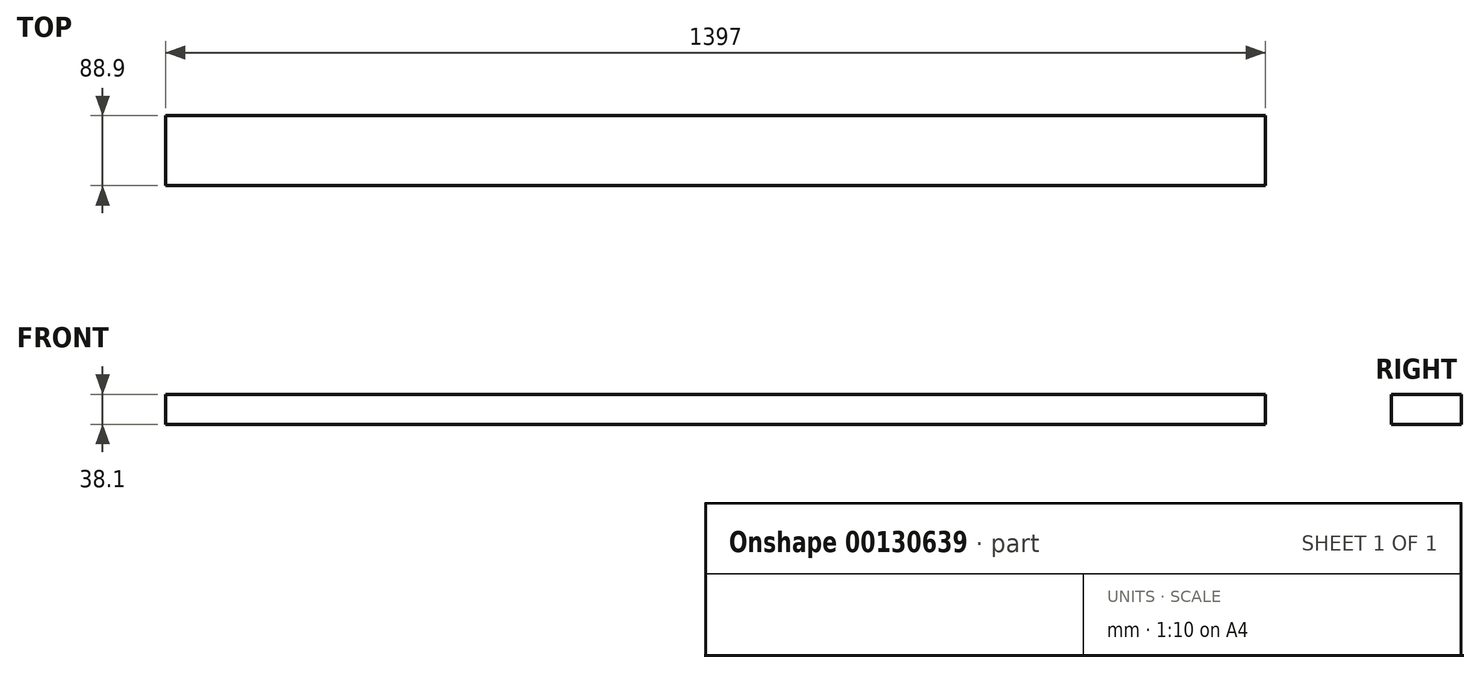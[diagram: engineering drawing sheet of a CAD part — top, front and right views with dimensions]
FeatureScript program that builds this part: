
annotation { "Feature Type Name" : "Feature", "Feature Type Description" : "" }
export const myFeature = defineFeature(function(context is Context, id is Id, definition is map)
    precondition{}
    {
        {
            var Q0;
            Q0=qCreatedBy(makeId("Top.planeOp"),FACE);
            var sketch = newSketch(context, id + "F0", { "sketchPlane" : qUnion([Q0])});
            skLineSegment(sketch, "E0.bottom", {"start": v(0, 0) * mm, "end": v(1397, 0) * mm});
            skLineSegment(sketch, "E0.top", {"start": v(0, 88.9) * mm, "end": v(1397, 88.9) * mm});
            skLineSegment(sketch, "E0.left", {"start": v(0, 0) * mm, "end": v(0, 88.9) * mm});
            skLineSegment(sketch, "E0.right", {"start": v(1397, 0) * mm, "end": v(1397, 88.9) * mm});
            skSolve(sketch);
        }
        {
            var Q0;
            Q0=makeQuery(id+"F0.imprint","IMPRINT",FACE,{"disambiguationData":[TD([[makeQuery(id+"F0.imprint","IMPRINT",EDGE,{"derivedFrom":sQuery(id+"F0.wireOp",EDGE,"E0.bottom")}),1.0]])]});
            extrude(context, id + "F1", {"entities" : qUnion([Q0]), "depth" : 38.1 * mm});
        }
    });
